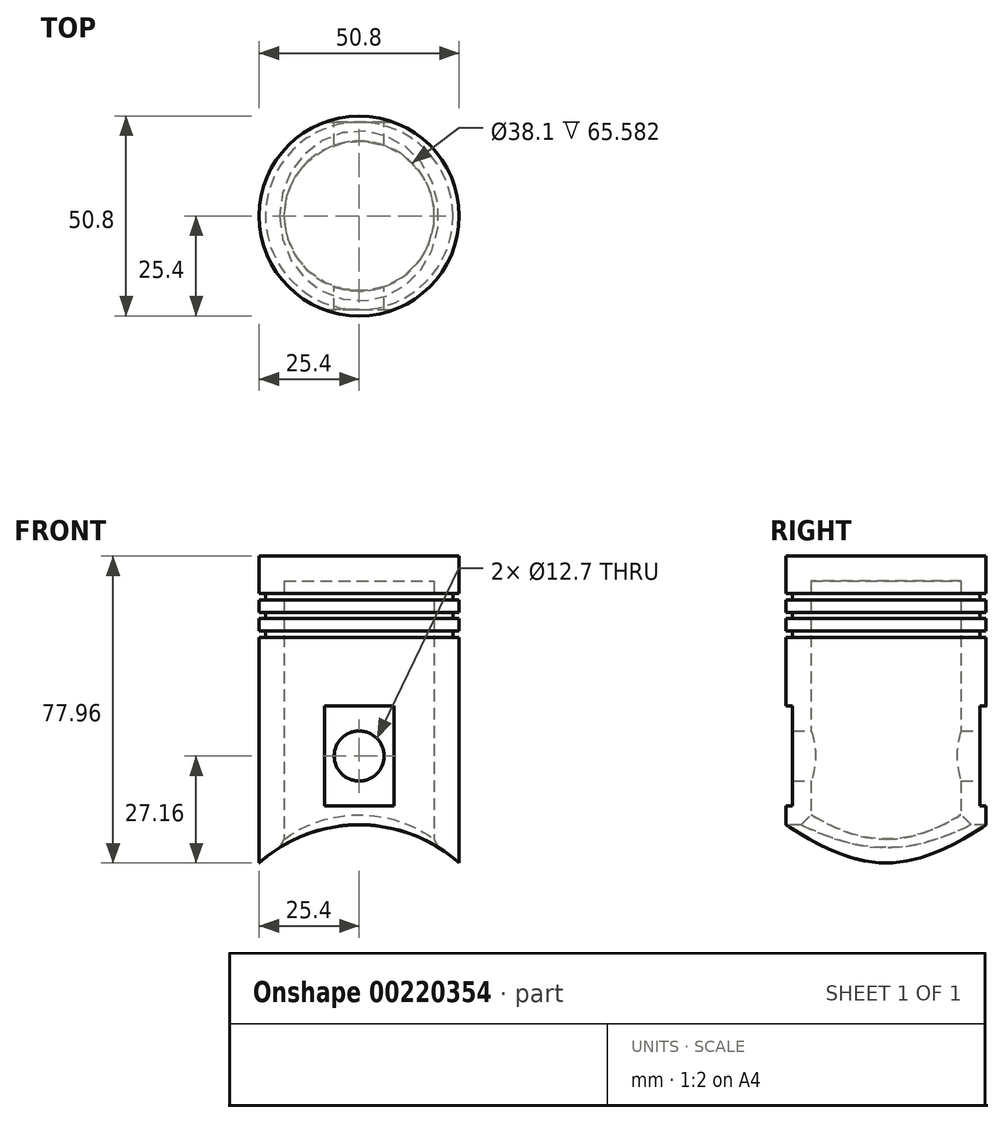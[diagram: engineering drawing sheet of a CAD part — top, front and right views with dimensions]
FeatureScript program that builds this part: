
annotation { "Feature Type Name" : "Feature", "Feature Type Description" : "" }
export const myFeature = defineFeature(function(context is Context, id is Id, definition is map)
    precondition{}
    {
        {
            var Q0;
            Q0=qCreatedBy(makeId("Front.planeOp"),FACE);
            var sketch = newSketch(context, id + "F0", { "sketchPlane" : qUnion([Q0])});
            skLineSegment(sketch, "E0", {"start": v(0, 76.2) * mm, "end": v(-25.4, 76.2) * mm});
            skLineSegment(sketch, "E1", {"start": v(-25.4, 76.2) * mm, "end": v(-25.4, 66.67) * mm});
            skLineSegment(sketch, "E2", {"start": v(-25.4, 66.67) * mm, "end": v(-23.81, 66.67) * mm});
            skLineSegment(sketch, "E3", {"start": v(-23.81, 66.67) * mm, "end": v(-23.81, 65.09) * mm});
            skLineSegment(sketch, "E4", {"start": v(-23.81, 65.09) * mm, "end": v(-25.4, 65.09) * mm});
            skLineSegment(sketch, "E5", {"start": v(-25.4, 65.09) * mm, "end": v(-25.4, 61.91) * mm});
            skLineSegment(sketch, "E6", {"start": v(-25.4, 61.91) * mm, "end": v(-23.81, 61.91) * mm});
            skLineSegment(sketch, "E7", {"start": v(-23.81, 61.91) * mm, "end": v(-23.81, 60.32) * mm});
            skLineSegment(sketch, "E8", {"start": v(-23.81, 60.32) * mm, "end": v(-25.4, 60.32) * mm});
            skLineSegment(sketch, "E9", {"start": v(-25.4, 60.32) * mm, "end": v(-25.4, 57.15) * mm});
            skLineSegment(sketch, "E10", {"start": v(-25.4, 57.15) * mm, "end": v(-23.81, 57.15) * mm});
            skLineSegment(sketch, "E11", {"start": v(-23.81, 57.15) * mm, "end": v(-23.81, 55.56) * mm});
            skLineSegment(sketch, "E12", {"start": v(-23.81, 55.56) * mm, "end": v(-25.4, 55.56) * mm});
            skLineSegment(sketch, "E13", {"start": v(-25.4, 55.56) * mm, "end": v(-25.4, -7.94) * mm});
            skLineSegment(sketch, "E14", {"start": v(-25.4, -7.94) * mm, "end": v(-19.05, -7.94) * mm});
            skLineSegment(sketch, "E15", {"start": v(-19.05, -7.94) * mm, "end": v(-19.05, 69.85) * mm});
            skLineSegment(sketch, "E16", {"start": v(-19.05, 69.85) * mm, "end": v(0, 69.85) * mm});
            skLineSegment(sketch, "E17", {"start": v(0, 69.85) * mm, "end": v(0, 76.2) * mm});
            skLineSegment(sketch, "E18", {"start": v(0, 0) * mm, "end": v(25.4, 0) * mm, "construction": true});
            skLineSegment(sketch, "E19", {"start": v(0, 0) * mm, "end": v(0, 42.58) * mm, "construction": true});
            skSolve(sketch);
        }
        {
            var Q0;
            Q0 = qSketchRegion(id + "F0", true);
            var Q1;
            Q1=sQuery(id+"F0.wireOp",EDGE,"E19");
            revolve(context, id + "F1", {"entities" : qUnion([Q0]), "axis" : qUnion([Q1]), "revolveType" : RevolveType.FULL});
        }
        {
            var Q0;
            Q0=qCreatedBy(makeId("Front.planeOp"),FACE);
            var sketch = newSketch(context, id + "F2", { "sketchPlane" : qUnion([Q0])});
            skCircle(sketch, "E20", {"center": v(0, -30.16) * mm, "radius": 38.1 * mm});
            skSolve(sketch);
        }
        {
            var Q0;
            Q0=makeQuery(id+"F2.imprint","IMPRINT",FACE,{"disambiguationData":[TD([[makeQuery(id+"F2.imprint","IMPRINT",EDGE,{"derivedFrom":sQuery(id+"F2.wireOp",EDGE,"E20")}),1.0]])]});
            extrude(context, id + "F3", {"entities" : qUnion([Q0]), "operationType" : NewBodyOperationType.REMOVE, "endBound" : BoundingType.SYMMETRIC, "oppositeDirection" : true, "depth" : 161.04 * mm});
        }
        {
            var Q0;
            Q0=qCreatedBy(makeId("Right.planeOp"),FACE);
            var sketch = newSketch(context, id + "F4", { "sketchPlane" : qUnion([Q0])});
            skLineSegment(sketch, "E21.bottom", {"start": v(-36.51, 38.1) * mm, "end": v(-23.81, 38.1) * mm});
            skLineSegment(sketch, "E21.top", {"start": v(-36.51, 12.7) * mm, "end": v(-23.81, 12.7) * mm});
            skLineSegment(sketch, "E21.left", {"start": v(-36.51, 38.1) * mm, "end": v(-36.51, 12.7) * mm});
            skLineSegment(sketch, "E21.right", {"start": v(-23.81, 38.1) * mm, "end": v(-23.81, 12.7) * mm});
            skLineSegment(sketch, "E22.bottom", {"start": v(36.51, 38.1) * mm, "end": v(23.81, 38.1) * mm});
            skLineSegment(sketch, "E22.top", {"start": v(36.51, 12.7) * mm, "end": v(23.81, 12.7) * mm});
            skLineSegment(sketch, "E22.left", {"start": v(36.51, 38.1) * mm, "end": v(36.51, 12.7) * mm});
            skLineSegment(sketch, "E22.right", {"start": v(23.81, 38.1) * mm, "end": v(23.81, 12.7) * mm});
            skSolve(sketch);
        }
        {
            var Q0;
            Q0 = qSketchRegion(id + "F4", true);
            extrude(context, id + "F5", {"entities" : qUnion([Q0]), "operationType" : NewBodyOperationType.REMOVE, "endBound" : BoundingType.SYMMETRIC, "oppositeDirection" : true, "depth" : 142.75 * mm});
        }
        {
            var Q0;
            Q0=makeQuery(id+"F5.boolean.opBoolean","COPY",FACE,{"derivedFrom":makeQuery(id+"F5.opExtrude","SWEPT_FACE",FACE,{"disambiguationData":[OSD([sQuery(id+"F4.wireOp",EDGE,"E22.right")])]})});
            var sketch = newSketch(context, id + "F6", { "sketchPlane" : qUnion([Q0])});
            skCircle(sketch, "E23", {"center": v(0, 25.4) * mm, "radius": 6.35 * mm});
            skSolve(sketch);
        }
        {
            var Q0;
            Q0 = qSketchRegion(id + "F6", true);
            extrude(context, id + "F7", {"entities" : qUnion([Q0]), "operationType" : NewBodyOperationType.REMOVE, "oppositeDirection" : true, "depth" : 122.68 * mm});
        }
        {
            var Q0;
            Q0=makeQuery(id+"F3.boolean.opBoolean","INTERSECT",EDGE,{"derivedFrom":[makeQuery(id+"F1.opRevolve","SWEPT_FACE",FACE,{"disambiguationData":[OSD([sQuery(id+"F0.wireOp",EDGE,"E15")])]}),makeQuery(id+"F3.opExtrude","SWEPT_FACE",FACE,{"disambiguationData":[OSD([sQuery(id+"F2.wireOp",EDGE,"E20")])]})]});
            chamfer(context, id + "F8", {"entities" : qUnion([Q0]), "width" : 2.54 * mm, "tangentPropagation" : true});
        }
    });
